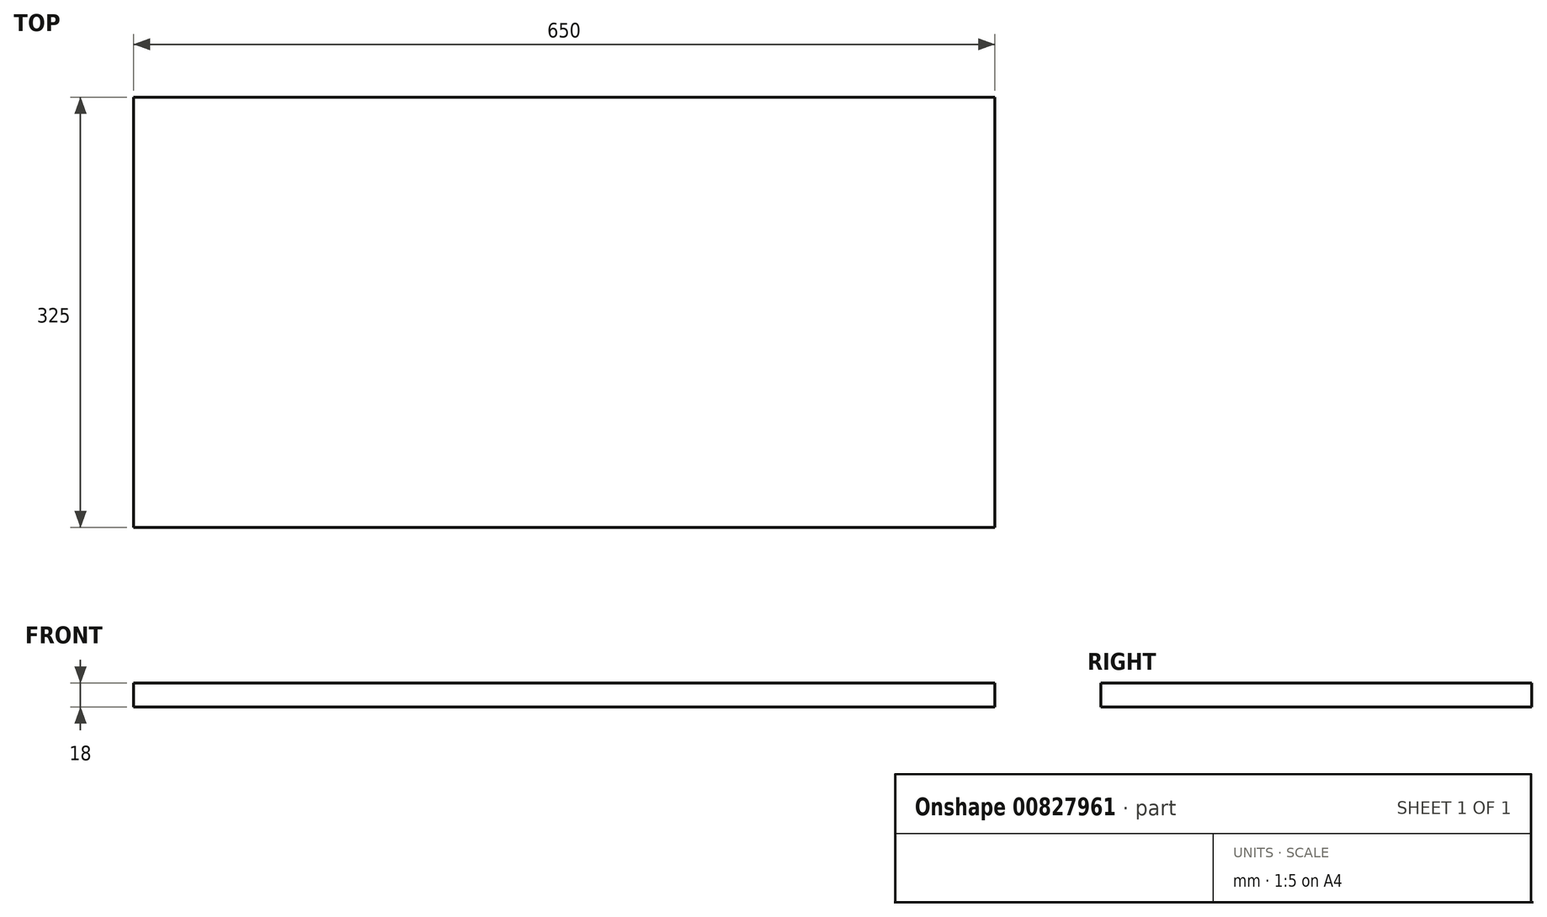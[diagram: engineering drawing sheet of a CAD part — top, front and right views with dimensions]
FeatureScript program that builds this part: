
annotation { "Feature Type Name" : "Feature", "Feature Type Description" : "" }
export const myFeature = defineFeature(function(context is Context, id is Id, definition is map)
    precondition{}
    {
        {
            var Q0;
            Q0=qCreatedBy(makeId("Top.planeOp"),FACE);
            var sketch = newSketch(context, id + "F0", { "sketchPlane" : qUnion([Q0])});
            skLineSegment(sketch, "E0.bottom", {"start": v(-325, 162.5) * mm, "end": v(325, 162.5) * mm});
            skLineSegment(sketch, "E0.top", {"start": v(-325, -162.5) * mm, "end": v(325, -162.5) * mm});
            skLineSegment(sketch, "E0.left", {"start": v(-325, 162.5) * mm, "end": v(-325, -162.5) * mm});
            skLineSegment(sketch, "E0.right", {"start": v(325, 162.5) * mm, "end": v(325, -162.5) * mm});
            skPoint(sketch, "E0.middle", {"position": v(0, 0) * mm});
            skSolve(sketch);
        }
        {
            var Q0;
            Q0=makeQuery(id+"F0.imprint","IMPRINT",FACE,{"disambiguationData":[TD([[makeQuery(id+"F0.imprint","IMPRINT",EDGE,{"derivedFrom":sQuery(id+"F0.wireOp",EDGE,"E0.bottom")}),-1.0]])]});
            extrude(context, id + "F1", {"entities" : qUnion([Q0]), "depth" : 18 * mm, "offsetDistance" : 25 * mm});
        }
    });
